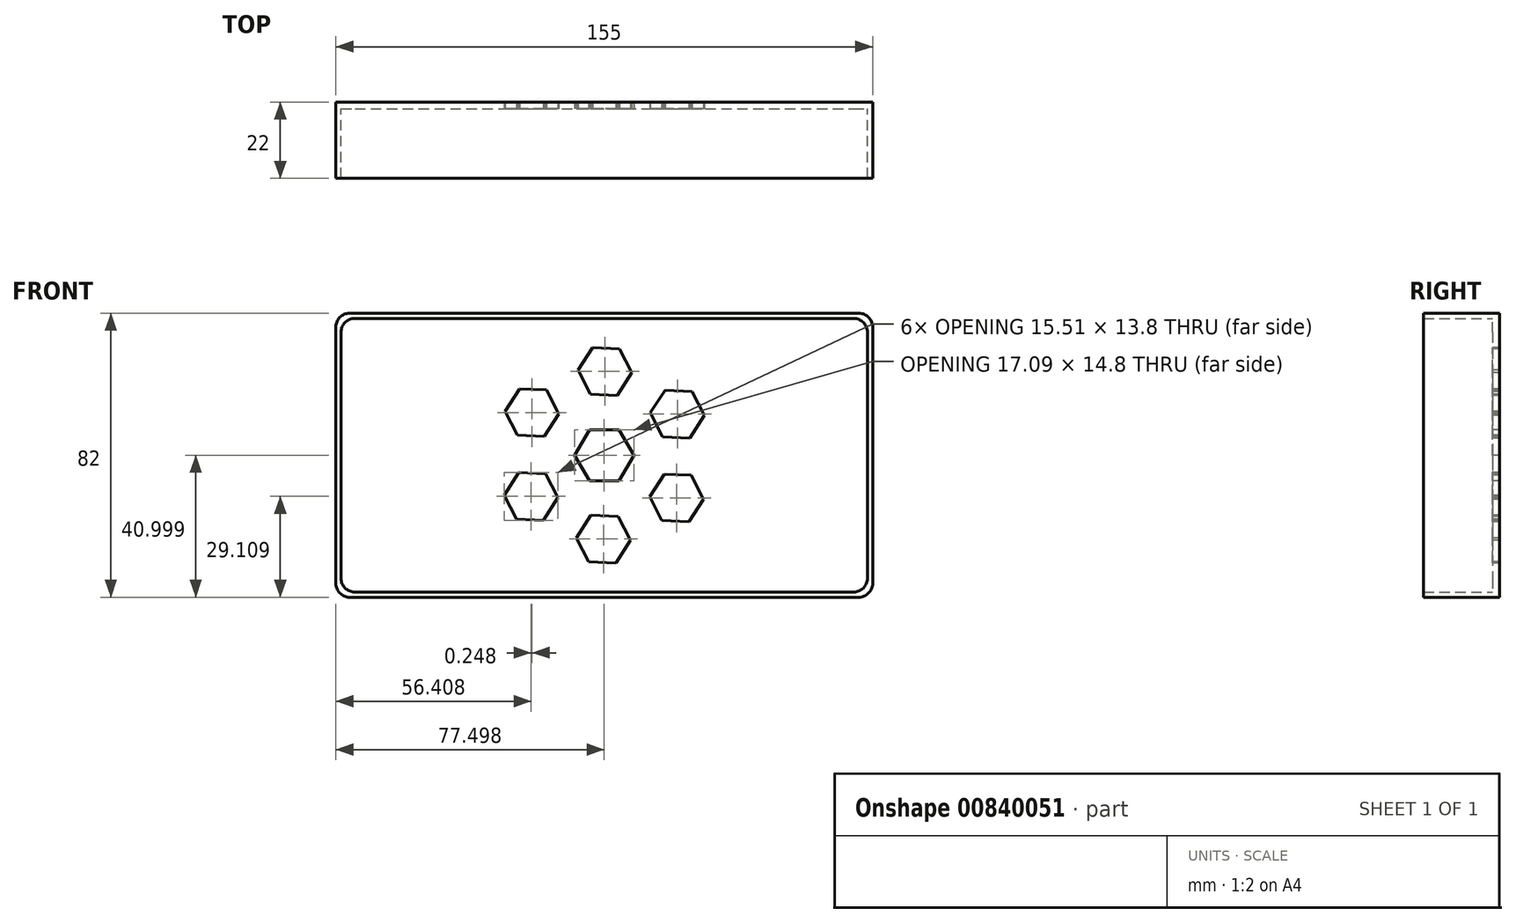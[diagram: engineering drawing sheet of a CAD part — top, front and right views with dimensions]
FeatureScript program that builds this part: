
annotation { "Feature Type Name" : "Feature", "Feature Type Description" : "" }
export const myFeature = defineFeature(function(context is Context, id is Id, definition is map)
    precondition{}
    {
        {
            var Q0;
            Q0=qCreatedBy(makeId("Front.planeOp"),FACE);
            var sketch = newSketch(context, id + "F0", { "sketchPlane" : qUnion([Q0])});
            skLineSegment(sketch, "E0.bottom", {"start": v(-67.12, 46) * mm, "end": v(79.88, 46) * mm});
            skLineSegment(sketch, "E0.top", {"start": v(-67.12, -36) * mm, "end": v(79.88, -36) * mm});
            skLineSegment(sketch, "E0.left", {"start": v(-71.12, 42) * mm, "end": v(-71.12, -32) * mm});
            skLineSegment(sketch, "E0.right", {"start": v(83.88, 42) * mm, "end": v(83.88, -32) * mm});
            skPoint(sketch, "E1.visualSharp", {"position": v(-71.12, 46) * mm});
            skArc(sketch, "E1.filletArc", {"start": v(-67.12, 46) * mm, "mid": v(-69.95, 44.83) * mm, "end": v(-71.12, 42) * mm});
            skPoint(sketch, "E2.visualSharp", {"position": v(-71.12, -36) * mm});
            skArc(sketch, "E2.filletArc", {"start": v(-71.12, -32) * mm, "mid": v(-69.95, -34.83) * mm, "end": v(-67.12, -36) * mm});
            skPoint(sketch, "E3.visualSharp", {"position": v(83.88, 46) * mm});
            skArc(sketch, "E3.filletArc", {"start": v(83.88, 42) * mm, "mid": v(82.7, 44.83) * mm, "end": v(79.88, 46) * mm});
            skPoint(sketch, "E4.visualSharp", {"position": v(83.88, -36) * mm});
            skArc(sketch, "E4.filletArc", {"start": v(79.88, -36) * mm, "mid": v(82.7, -34.83) * mm, "end": v(83.88, -32) * mm});
            skSolve(sketch);
        }
        {
            var Q0;
            Q0=makeQuery(id+"F0.imprint","IMPRINT",FACE,{"disambiguationData":[TD([[makeQuery(id+"F0.imprint","IMPRINT",EDGE,{"derivedFrom":sQuery(id+"F0.wireOp",EDGE,"E0.bottom")}),-1.0]])]});
            extrude(context, id + "F1", {"entities" : qUnion([Q0]), "depth" : 2 * mm, "offsetDistance" : 25 * mm});
        }
        {
            var Q0;
            Q0=makeQuery(id+"F1.opExtrude","CAP_FACE",FACE,{"disambiguationData":[OSD([sQuery(id+"F0.wireOp",EDGE,"E0.bottom"),sQuery(id+"F0.wireOp",EDGE,"E0.top"),sQuery(id+"F0.wireOp",EDGE,"E0.left"),sQuery(id+"F0.wireOp",EDGE,"E0.right"),sQuery(id+"F0.wireOp",EDGE,"E1.filletArc"),sQuery(id+"F0.wireOp",EDGE,"E2.filletArc"),sQuery(id+"F0.wireOp",EDGE,"E3.filletArc"),sQuery(id+"F0.wireOp",EDGE,"E4.filletArc")])],"isStart":false});
            var sketch = newSketch(context, id + "F2", { "sketchPlane" : qUnion([Q0])});
            skLineSegment(sketch, "E5.bottom", {"start": v(-65.62, 44.5) * mm, "end": v(78.38, 44.5) * mm});
            skLineSegment(sketch, "E5.top", {"start": v(-65.62, -34.5) * mm, "end": v(78.38, -34.5) * mm});
            skLineSegment(sketch, "E5.left", {"start": v(-69.62, 40.5) * mm, "end": v(-69.62, -30.5) * mm});
            skLineSegment(sketch, "E5.right", {"start": v(82.38, 40.5) * mm, "end": v(82.38, -30.5) * mm});
            skPoint(sketch, "E6.visualSharp", {"position": v(-69.62, 44.5) * mm});
            skArc(sketch, "E6.filletArc", {"start": v(-65.62, 44.5) * mm, "mid": v(-68.45, 43.33) * mm, "end": v(-69.62, 40.5) * mm});
            skPoint(sketch, "E7.visualSharp", {"position": v(-69.62, -34.5) * mm});
            skArc(sketch, "E7.filletArc", {"start": v(-69.62, -30.5) * mm, "mid": v(-68.45, -33.33) * mm, "end": v(-65.62, -34.5) * mm});
            skPoint(sketch, "E8.visualSharp", {"position": v(82.38, -34.5) * mm});
            skArc(sketch, "E8.filletArc", {"start": v(78.38, -34.5) * mm, "mid": v(81.2, -33.33) * mm, "end": v(82.38, -30.5) * mm});
            skPoint(sketch, "E9.visualSharp", {"position": v(82.38, 44.5) * mm});
            skArc(sketch, "E9.filletArc", {"start": v(82.38, 40.5) * mm, "mid": v(81.2, 43.33) * mm, "end": v(78.38, 44.5) * mm});
            skSolve(sketch);
        }
        {
            var Q0;
            Q0=makeQuery(id+"F2.imprint","IMPRINT",FACE,{"disambiguationData":[TD([[makeQuery(id+"F2.imprint","IMPRINT",EDGE,{"derivedFrom":sQuery(id+"F2.wireOp",EDGE,"E5.bottom")}),1.0]])]});
            extrude(context, id + "F3", {"entities" : qUnion([Q0]), "operationType" : NewBodyOperationType.ADD, "depth" : 20 * mm, "offsetDistance" : 25 * mm});
        }
        {
            var Q0;
            Q0=makeQuery(id+"F1.opExtrude","CAP_FACE",FACE,{"disambiguationData":[OSD([sQuery(id+"F0.wireOp",EDGE,"E0.bottom"),sQuery(id+"F0.wireOp",EDGE,"E0.top"),sQuery(id+"F0.wireOp",EDGE,"E0.left"),sQuery(id+"F0.wireOp",EDGE,"E0.right"),sQuery(id+"F0.wireOp",EDGE,"E1.filletArc"),sQuery(id+"F0.wireOp",EDGE,"E2.filletArc"),sQuery(id+"F0.wireOp",EDGE,"E3.filletArc"),sQuery(id+"F0.wireOp",EDGE,"E4.filletArc")])],"isStart":false});
            var sketch = newSketch(context, id + "F4", { "sketchPlane" : qUnion([Q0])});
            skCircle(sketch, "E10", {"center": v(6.38, 5) * mm, "radius": 24.21 * mm, "construction": true});
            skPoint(sketch, "E10.centerSnap0", {"position": v(82.38, 5) * mm});
            skPoint(sketch, "E10.centerSnap1", {"position": v(6.38, 44.5) * mm});
            skLineSegment(sketch, "E11.0", {"start": v(10.83, 35.74) * mm, "end": v(14.38, 28.84) * mm});
            skLineSegment(sketch, "E11.1", {"start": v(14.38, 28.84) * mm, "end": v(10.18, 22.3) * mm});
            skLineSegment(sketch, "E11.2", {"start": v(10.18, 22.3) * mm, "end": v(2.43, 22.68) * mm});
            skLineSegment(sketch, "E11.3", {"start": v(2.43, 22.68) * mm, "end": v(-1.13, 29.58) * mm});
            skLineSegment(sketch, "E11.4", {"start": v(-1.13, 29.58) * mm, "end": v(3.07, 36.1) * mm});
            skLineSegment(sketch, "E11.5", {"start": v(3.07, 36.1) * mm, "end": v(10.83, 35.74) * mm});
            skPoint(sketch, "E11.0.midPoint", {"position": v(12.6, 32.29) * mm});
            skLineSegment(sketch, "E12.1.0", {"start": v(-22.22, 17.7) * mm, "end": v(-18.02, 24.22) * mm});
            skLineSegment(sketch, "E12.1.1", {"start": v(-18.66, 10.79) * mm, "end": v(-22.22, 17.7) * mm});
            skLineSegment(sketch, "E12.1.2", {"start": v(-10.9, 10.42) * mm, "end": v(-18.66, 10.79) * mm});
            skLineSegment(sketch, "E12.1.3", {"start": v(-6.7, 16.95) * mm, "end": v(-10.9, 10.42) * mm});
            skLineSegment(sketch, "E12.1.4", {"start": v(-10.26, 23.85) * mm, "end": v(-6.7, 16.95) * mm});
            skLineSegment(sketch, "E12.1.5", {"start": v(-18.02, 24.22) * mm, "end": v(-10.26, 23.85) * mm});
            skLineSegment(sketch, "E12.2.0", {"start": v(-18.91, -13.42) * mm, "end": v(-22.47, -6.52) * mm});
            skLineSegment(sketch, "E12.2.1", {"start": v(-11.16, -13.8) * mm, "end": v(-18.91, -13.42) * mm});
            skLineSegment(sketch, "E12.2.2", {"start": v(-6.96, -7.26) * mm, "end": v(-11.16, -13.8) * mm});
            skLineSegment(sketch, "E12.2.3", {"start": v(-10.51, -0.36) * mm, "end": v(-6.96, -7.26) * mm});
            skLineSegment(sketch, "E12.2.4", {"start": v(-18.27, 0.01) * mm, "end": v(-10.51, -0.36) * mm});
            skLineSegment(sketch, "E12.2.5", {"start": v(-22.47, -6.52) * mm, "end": v(-18.27, 0.01) * mm});
            skLineSegment(sketch, "E12.3.0", {"start": v(9.68, -26.11) * mm, "end": v(1.93, -25.74) * mm});
            skLineSegment(sketch, "E12.3.1", {"start": v(13.88, -19.58) * mm, "end": v(9.68, -26.11) * mm});
            skLineSegment(sketch, "E12.3.2", {"start": v(10.33, -12.68) * mm, "end": v(13.88, -19.58) * mm});
            skLineSegment(sketch, "E12.3.3", {"start": v(2.57, -12.3) * mm, "end": v(10.33, -12.68) * mm});
            skLineSegment(sketch, "E12.3.4", {"start": v(-1.63, -18.84) * mm, "end": v(2.57, -12.3) * mm});
            skLineSegment(sketch, "E12.3.5", {"start": v(1.93, -25.74) * mm, "end": v(-1.63, -18.84) * mm});
            skLineSegment(sketch, "E12.4.0", {"start": v(34.97, -7.7) * mm, "end": v(30.77, -14.22) * mm});
            skLineSegment(sketch, "E12.4.1", {"start": v(31.42, -0.8) * mm, "end": v(34.97, -7.7) * mm});
            skLineSegment(sketch, "E12.4.2", {"start": v(23.66, -0.42) * mm, "end": v(31.42, -0.8) * mm});
            skLineSegment(sketch, "E12.4.3", {"start": v(19.46, -6.95) * mm, "end": v(23.66, -0.42) * mm});
            skLineSegment(sketch, "E12.4.4", {"start": v(23.02, -13.85) * mm, "end": v(19.46, -6.95) * mm});
            skLineSegment(sketch, "E12.4.5", {"start": v(30.77, -14.22) * mm, "end": v(23.02, -13.85) * mm});
            skLineSegment(sketch, "E12.5.0", {"start": v(31.67, 23.42) * mm, "end": v(35.22, 16.52) * mm});
            skLineSegment(sketch, "E12.5.1", {"start": v(23.91, 23.8) * mm, "end": v(31.67, 23.42) * mm});
            skLineSegment(sketch, "E12.5.2", {"start": v(19.71, 17.26) * mm, "end": v(23.91, 23.8) * mm});
            skLineSegment(sketch, "E12.5.3", {"start": v(23.27, 10.36) * mm, "end": v(19.71, 17.26) * mm});
            skLineSegment(sketch, "E12.5.4", {"start": v(31.02, 9.99) * mm, "end": v(23.27, 10.36) * mm});
            skLineSegment(sketch, "E12.5.5", {"start": v(35.22, 16.52) * mm, "end": v(31.02, 9.99) * mm});
            skCircle(sketch, "E13.cCircle", {"center": v(6.38, 5) * mm, "radius": 7.4 * mm, "construction": true});
            skLineSegment(sketch, "E13.0", {"start": v(10.65, -2.4) * mm, "end": v(2.1, -2.4) * mm});
            skLineSegment(sketch, "E13.1", {"start": v(2.1, -2.4) * mm, "end": v(-2.17, 5) * mm});
            skLineSegment(sketch, "E13.2", {"start": v(-2.17, 5) * mm, "end": v(2.1, 12.4) * mm});
            skLineSegment(sketch, "E13.3", {"start": v(2.1, 12.4) * mm, "end": v(10.65, 12.4) * mm});
            skLineSegment(sketch, "E13.4", {"start": v(10.65, 12.4) * mm, "end": v(14.92, 5) * mm});
            skLineSegment(sketch, "E13.5", {"start": v(14.92, 5) * mm, "end": v(10.65, -2.4) * mm});
            skPoint(sketch, "E13.0.midPoint", {"position": v(6.38, -2.4) * mm});
            skSolve(sketch);
        }
        {
            var Q0;
            Q0=makeQuery(id+"F4.imprint","IMPRINT",FACE,{"disambiguationData":[TD([[makeQuery(id+"F4.imprint","IMPRINT",EDGE,{"derivedFrom":sQuery(id+"F4.wireOp",EDGE,"E11.0")}),-1.0]])]});
            var Q1;
            Q1=makeQuery(id+"F4.imprint","IMPRINT",FACE,{"disambiguationData":[TD([[makeQuery(id+"F4.imprint","IMPRINT",EDGE,{"derivedFrom":sQuery(id+"F4.wireOp",EDGE,"E12.7.0")}),-1.0]])]});
            var Q2;
            Q2=makeQuery(id+"F4.imprint","IMPRINT",FACE,{"disambiguationData":[TD([[makeQuery(id+"F4.imprint","IMPRINT",EDGE,{"derivedFrom":sQuery(id+"F4.wireOp",EDGE,"E12.6.0")}),-1.0]])]});
            var Q3;
            Q3=makeQuery(id+"F4.imprint","IMPRINT",FACE,{"disambiguationData":[TD([[makeQuery(id+"F4.imprint","IMPRINT",EDGE,{"derivedFrom":sQuery(id+"F4.wireOp",EDGE,"E12.5.0")}),-1.0]])]});
            var Q4;
            Q4=makeQuery(id+"F4.imprint","IMPRINT",FACE,{"disambiguationData":[TD([[makeQuery(id+"F4.imprint","IMPRINT",EDGE,{"derivedFrom":sQuery(id+"F4.wireOp",EDGE,"E12.4.0")}),-1.0]])]});
            var Q5;
            Q5=makeQuery(id+"F4.imprint","IMPRINT",FACE,{"disambiguationData":[TD([[makeQuery(id+"F4.imprint","IMPRINT",EDGE,{"derivedFrom":sQuery(id+"F4.wireOp",EDGE,"E12.3.0")}),-1.0]])]});
            var Q6;
            Q6=makeQuery(id+"F4.imprint","IMPRINT",FACE,{"disambiguationData":[TD([[makeQuery(id+"F4.imprint","IMPRINT",EDGE,{"derivedFrom":sQuery(id+"F4.wireOp",EDGE,"E12.2.0")}),-1.0]])]});
            var Q7;
            Q7=makeQuery(id+"F4.imprint","IMPRINT",FACE,{"disambiguationData":[TD([[makeQuery(id+"F4.imprint","IMPRINT",EDGE,{"derivedFrom":sQuery(id+"F4.wireOp",EDGE,"E12.1.0")}),-1.0]])]});
            var Q8;
            Q8=makeQuery(id+"F4.imprint","IMPRINT",FACE,{"disambiguationData":[TD([[makeQuery(id+"F4.imprint","IMPRINT",EDGE,{"derivedFrom":sQuery(id+"F4.wireOp",EDGE,"E13.0")}),-1.0]])]});
            extrude(context, id + "F5", {"entities" : qUnion([Q0, Q1, Q2, Q3, Q4, Q5, Q6, Q7, Q8]), "operationType" : NewBodyOperationType.REMOVE, "endBound" : BoundingType.SYMMETRIC, "oppositeDirection" : true, "depth" : 25 * mm, "offsetDistance" : 25 * mm});
        }
    });
